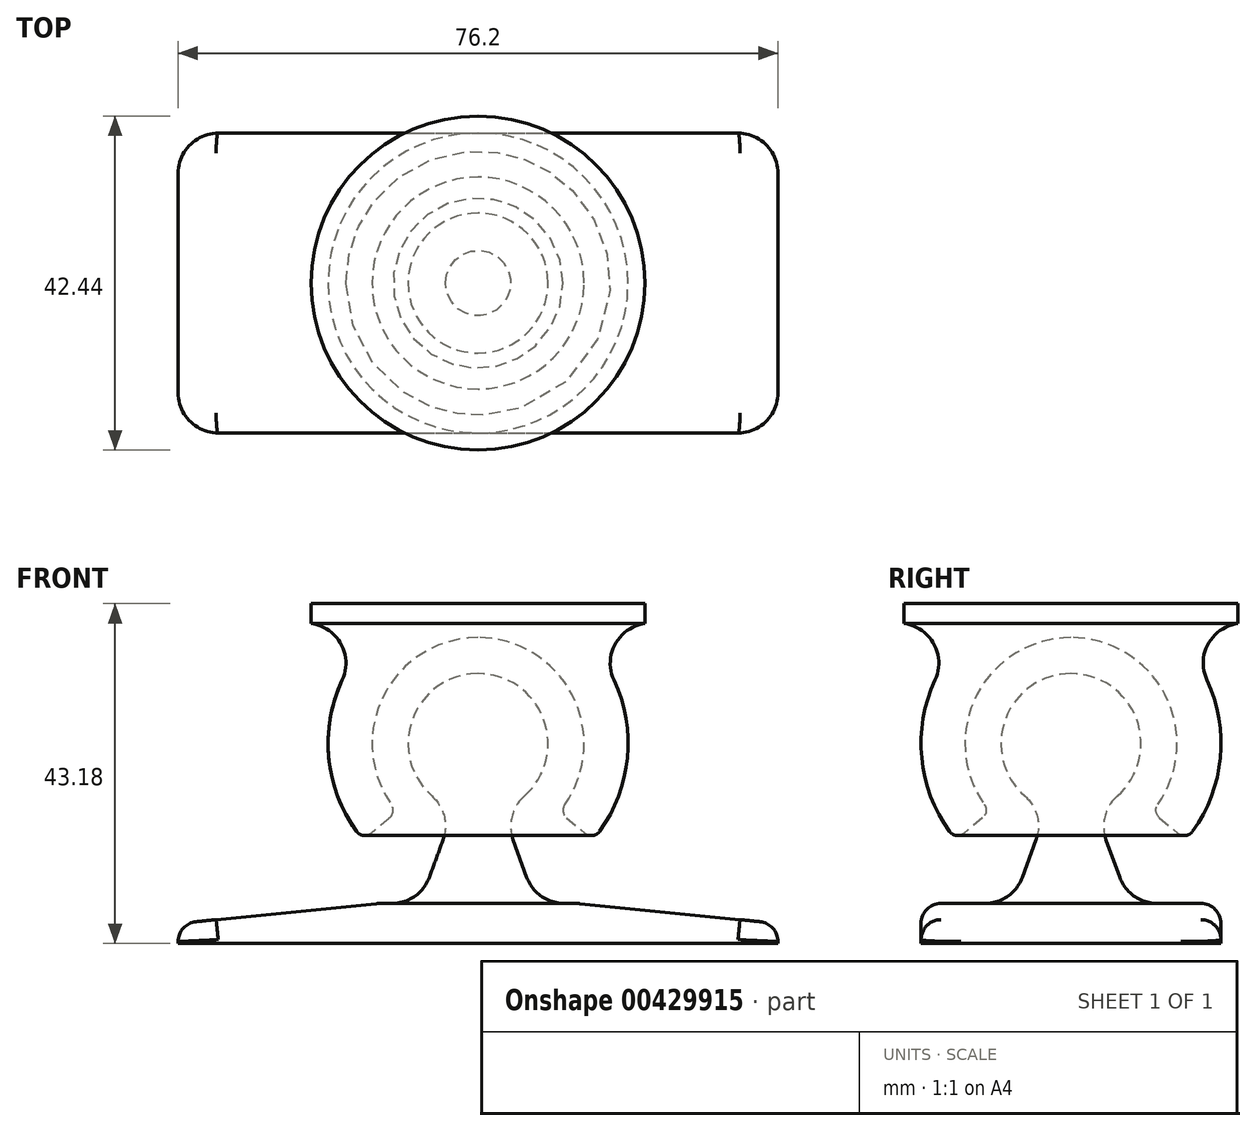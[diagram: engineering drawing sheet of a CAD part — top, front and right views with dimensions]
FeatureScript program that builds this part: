
annotation { "Feature Type Name" : "Feature", "Feature Type Description" : "" }
export const myFeature = defineFeature(function(context is Context, id is Id, definition is map)
    precondition{}
    {
        {
            var Q0;
            Q0=qCreatedBy(makeId("Front.planeOp"),FACE);
            var sketch = newSketch(context, id + "F0", { "sketchPlane" : qUnion([Q0])});
            skArc(sketch, "E0", {"start": v(0, 8.9) * mm, "mid": v(-8.75, 1.54) * mm, "end": v(-3.04, -8.35) * mm});
            skLineSegment(sketch, "E1", {"start": v(0, 0) * mm, "end": v(0, 52.78) * mm, "construction": true});
            skLineSegment(sketch, "E2", {"start": v(0, 8.9) * mm, "end": v(0, -22.86) * mm});
            skLineSegment(sketch, "E3", {"start": v(-12.7, -20.32) * mm, "end": v(-7.4, -20.32) * mm});
            skLineSegment(sketch, "E4", {"start": v(-3.04, -8.35) * mm, "end": v(-7.4, -20.32) * mm});
            skLineSegment(sketch, "E5.bottom", {"start": v(0, -22.86) * mm, "end": v(-12.7, -22.86) * mm});
            skLineSegment(sketch, "E5.right", {"start": v(-12.7, -22.86) * mm, "end": v(-12.7, -20.32) * mm});
            skArc(sketch, "E6", {"start": v(0, 13.46) * mm, "mid": v(-13.46, 0) * mm, "end": v(0, -13.46) * mm, "construction": true});
            skLineSegment(sketch, "E7", {"start": v(0, 0) * mm, "end": v(-14.6, -12.25) * mm, "construction": true});
            skArc(sketch, "E8", {"start": v(-11.43, 15.24) * mm, "mid": v(-18.07, -6.02) * mm, "end": v(0, -19.05) * mm, "construction": true});
            skLineSegment(sketch, "E9", {"start": v(-21.22, 17.78) * mm, "end": v(0, 17.78) * mm, "construction": true});
            skLineSegment(sketch, "E10", {"start": v(-21.22, 17.78) * mm, "end": v(-21.22, 15.24) * mm, "construction": true});
            skLineSegment(sketch, "E11", {"start": v(-21.22, 15.24) * mm, "end": v(-11.43, 15.24) * mm, "construction": true});
            skLineSegment(sketch, "E12", {"start": v(0, -22.86) * mm, "end": v(12.7, -22.86) * mm, "construction": true});
            skLineSegment(sketch, "E13", {"start": v(12.7, -22.86) * mm, "end": v(12.7, -20.32) * mm, "construction": true});
            skLineSegment(sketch, "E14", {"start": v(12.7, -20.32) * mm, "end": v(-7.4, -20.32) * mm, "construction": true});
            skSolve(sketch);
        }
        {
            var Q0;
            Q0 = qSketchRegion(id + "F0", true);
            var Q1;
            Q1=sQuery(id+"F0.wireOp",EDGE,"E1");
            revolve(context, id + "F1", {"entities" : qUnion([Q0]), "axis" : qUnion([Q1]), "revolveType" : RevolveType.FULL});
        }
        {
            var Q0;
            Q0=qCreatedBy(makeId("Front.planeOp"),FACE);
            var sketch = newSketch(context, id + "F2", { "sketchPlane" : qUnion([Q0])});
            skArc(sketch, "E15", {"start": v(0, 13.46) * mm, "mid": v(-12.2, 5.69) * mm, "end": v(-10.31, -8.65) * mm});
            skArc(sketch, "E16", {"start": v(-11.43, 15.24) * mm, "mid": v(-18.93, 2.18) * mm, "end": v(-14.6, -12.25) * mm});
            skLineSegment(sketch, "E17.bottom", {"start": v(-21.22, 17.78) * mm, "end": v(0, 17.78) * mm});
            skLineSegment(sketch, "E17.top", {"start": v(-21.22, 15.24) * mm, "end": v(-11.43, 15.24) * mm});
            skLineSegment(sketch, "E17.left", {"start": v(-21.22, 17.78) * mm, "end": v(-21.22, 15.24) * mm});
            skLineSegment(sketch, "E18", {"start": v(0, 17.78) * mm, "end": v(0, 13.46) * mm});
            skLineSegment(sketch, "E19", {"start": v(-10.31, -8.65) * mm, "end": v(-14.6, -12.25) * mm});
            skLineSegment(sketch, "E20", {"start": v(0, 17.78) * mm, "end": v(0, 26.9) * mm, "construction": true});
            skSolve(sketch);
        }
        {
            var Q0;
            Q0 = qSketchRegion(id + "F2", true);
            var Q1;
            Q1=sQuery(id+"F2.wireOp",EDGE,"E20");
            revolve(context, id + "F3", {"entities" : qUnion([Q0]), "axis" : qUnion([Q1]), "revolveType" : RevolveType.FULL});
        }
        {
            var Q0;
            Q0=makeQuery(id+"F3.opRevolve","SWEPT_EDGE",EDGE,{"disambiguationData":[OSD([sQuery(id+"F2.wireOp",EDGE,"E16"),sQuery(id+"F2.wireOp",EDGE,"E17.top")])]});
            var Q1;
            Q1=makeQuery(id+"F1.opRevolve","SWEPT_EDGE",EDGE,{"disambiguationData":[OSD([sQuery(id+"F0.wireOp",EDGE,"E3"),sQuery(id+"F0.wireOp",EDGE,"E4")])]});
            var Q2;
            Q2=makeQuery(id+"F1.opRevolve","SWEPT_EDGE",EDGE,{"disambiguationData":[OSD([sQuery(id+"F0.wireOp",EDGE,"E0"),sQuery(id+"F0.wireOp",EDGE,"E4")])]});
            fillet(context, id + "F4", {"entities" : qUnion([Q0, Q1, Q2]), "radius" : 5.08 * mm, "tangentPropagation" : true, "allowEdgeOverflow" : false});
        }
        {
            var Q0;
            Q0=makeQuery(id+"F3.opRevolve","SWEPT_FACE",FACE,{"disambiguationData":[OSD([sQuery(id+"F2.wireOp",EDGE,"E19")])]});
            fillet(context, id + "F5", {"entities" : qUnion([Q0]), "radius" : 1.27 * mm, "tangentPropagation" : true, "allowEdgeOverflow" : false});
        }
        {
            var Q0;
            Q0=qCreatedBy(makeId("Front.planeOp"),FACE);
            var sketch = newSketch(context, id + "F6", { "sketchPlane" : qUnion([Q0])});
            skLineSegment(sketch, "E21.bottom", {"start": v(-12.7, -20.32) * mm, "end": v(12.7, -20.32) * mm});
            skLineSegment(sketch, "E21.top", {"start": v(-38.1, -25.4) * mm, "end": v(38.1, -25.4) * mm});
            skLineSegment(sketch, "E21.left", {"start": v(-38.1, -22.86) * mm, "end": v(-38.1, -25.4) * mm});
            skLineSegment(sketch, "E21.right", {"start": v(38.1, -22.86) * mm, "end": v(38.1, -25.4) * mm});
            skPoint(sketch, "E22", {"position": v(0, -25.4) * mm});
            skLineSegment(sketch, "E23", {"start": v(-38.1, -22.86) * mm, "end": v(-12.7, -20.32) * mm});
            skLineSegment(sketch, "E24", {"start": v(38.1, -22.86) * mm, "end": v(12.7, -20.32) * mm});
            skPoint(sketch, "E25.orphan", {"position": v(38.1, -20.32) * mm});
            skPoint(sketch, "E26.orphan", {"position": v(-38.1, -20.32) * mm});
            skSolve(sketch);
        }
        {
            var Q0;
            Q0 = qSketchRegion(id + "F6", true);
            extrude(context, id + "F7", {"entities" : qUnion([Q0]), "operationType" : NewBodyOperationType.ADD, "depth" : 19.05 * mm, "hasSecondDirection" : true, "secondDirectionOppositeDirection" : true, "secondDirectionDepth" : 19.05 * mm});
        }
        {
            var Q0;
            Q0=makeQuery(id+"F7.opExtrude","CAP_EDGE",EDGE,{"disambiguationData":[OSD([sQuery(id+"F6.wireOp",EDGE,"E21.right")])],"isStart":false});
            var Q1;
            Q1=makeQuery(id+"F7.opExtrude","CAP_EDGE",EDGE,{"disambiguationData":[OSD([sQuery(id+"F6.wireOp",EDGE,"E21.right")])],"isStart":true});
            var Q2;
            Q2=makeQuery(id+"F7.opExtrude","CAP_EDGE",EDGE,{"disambiguationData":[OSD([sQuery(id+"F6.wireOp",EDGE,"E21.left")])],"isStart":false});
            var Q3;
            Q3=makeQuery(id+"F7.opExtrude","CAP_EDGE",EDGE,{"disambiguationData":[OSD([sQuery(id+"F6.wireOp",EDGE,"E21.left")])],"isStart":true});
            var Q4;
            Q4=makeQuery(id+"F7.opExtrude","SWEPT_EDGE",EDGE,{"disambiguationData":[OSD([sQuery(id+"F6.wireOp",EDGE,"E21.bottom"),sQuery(id+"F6.wireOp",EDGE,"E23")])]});
            var Q5;
            Q5=makeQuery(id+"F7.opExtrude","SWEPT_EDGE",EDGE,{"disambiguationData":[OSD([sQuery(id+"F6.wireOp",EDGE,"E21.bottom"),sQuery(id+"F6.wireOp",EDGE,"E24")])]});
            fillet(context, id + "F8", {"entities" : qUnion([Q0, Q1, Q2, Q3, Q4, Q5]), "radius" : 5.08 * mm, "tangentPropagation" : true, "allowEdgeOverflow" : false});
        }
        {
            var Q0;
            Q0=makeQuery(id+"F7.opExtrude","CAP_EDGE",EDGE,{"disambiguationData":[OSD([sQuery(id+"F6.wireOp",EDGE,"E23")])],"isStart":false});
            fillet(context, id + "F9", {"entities" : qUnion([Q0]), "radius" : 2.54 * mm, "tangentPropagation" : true, "allowEdgeOverflow" : false});
        }
    });
